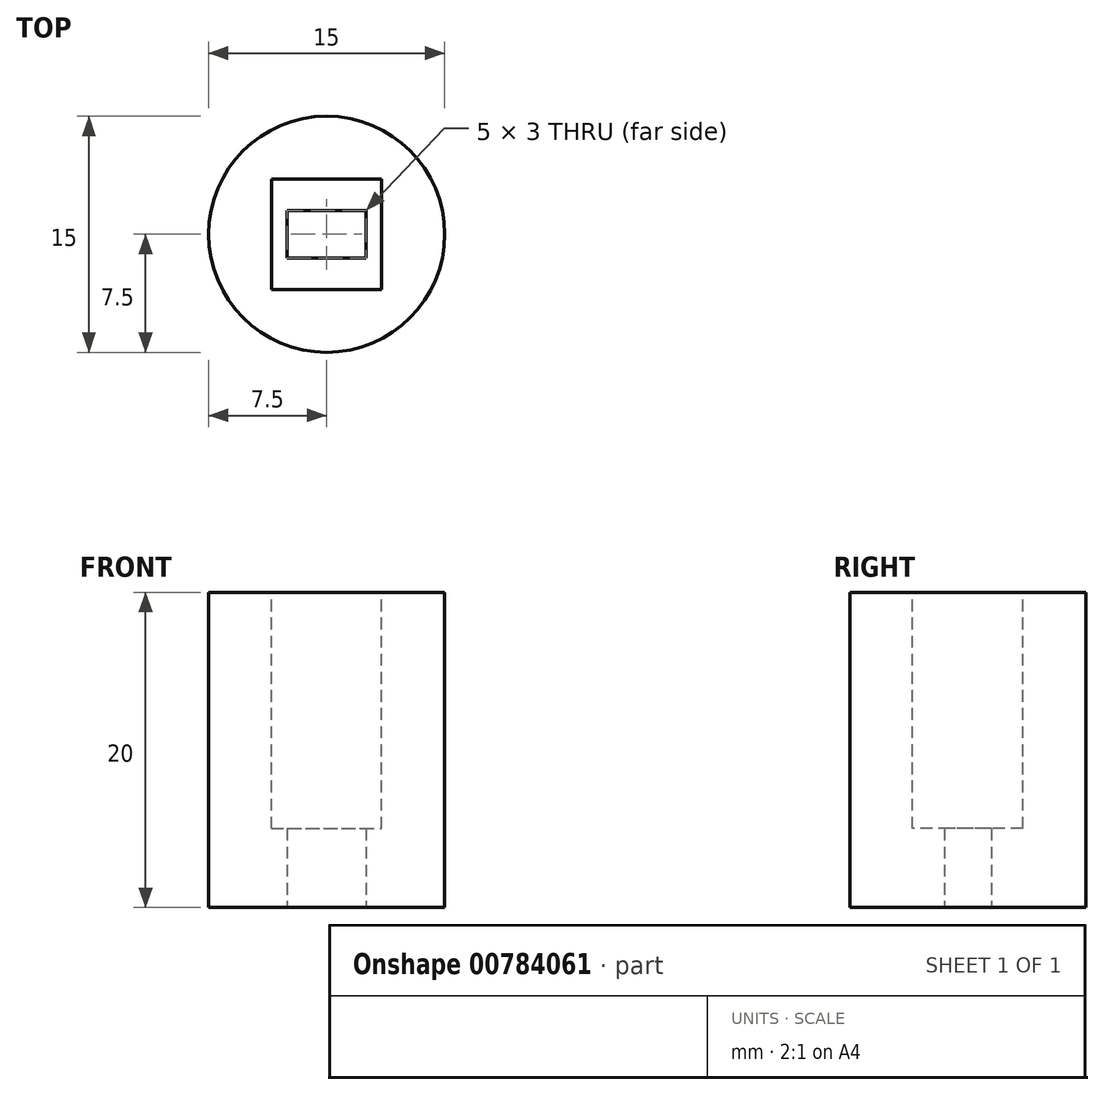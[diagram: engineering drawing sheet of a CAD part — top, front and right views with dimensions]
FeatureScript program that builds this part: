
annotation { "Feature Type Name" : "Feature", "Feature Type Description" : "" }
export const myFeature = defineFeature(function(context is Context, id is Id, definition is map)
    precondition{}
    {
        {
            var Q0;
            Q0=qCreatedBy(makeId("Top.planeOp"),FACE);
            var sketch = newSketch(context, id + "F0", { "sketchPlane" : qUnion([Q0])});
            skCircle(sketch, "E0", {"center": v(0, 0) * mm, "radius": 7.5 * mm});
            skLineSegment(sketch, "E1.bottom", {"start": v(-2.5, 1.5) * mm, "end": v(2.5, 1.5) * mm});
            skLineSegment(sketch, "E1.top", {"start": v(-2.5, -1.5) * mm, "end": v(2.5, -1.5) * mm});
            skLineSegment(sketch, "E1.left", {"start": v(-2.5, 1.5) * mm, "end": v(-2.5, -1.5) * mm});
            skLineSegment(sketch, "E1.right", {"start": v(2.5, 1.5) * mm, "end": v(2.5, -1.5) * mm});
            skSolve(sketch);
        }
        {
            var Q0;
            Q0=makeQuery(id+"F0.imprint","IMPRINT",FACE,{"disambiguationData":[TD([[makeQuery(id+"F0.imprint","IMPRINT",EDGE,{"derivedFrom":sQuery(id+"F0.wireOp",EDGE,"E0")}),1.0]])]});
            extrude(context, id + "F1", {"entities" : qUnion([Q0]), "depth" : 20 * mm, "offsetDistance" : 25 * mm});
        }
        {
            var Q0;
            Q0=makeQuery(id+"F1.opExtrude","CAP_FACE",FACE,{"disambiguationData":[OSD([sQuery(id+"F0.wireOp",EDGE,"E0"),sQuery(id+"F0.wireOp",EDGE,"E1.bottom"),sQuery(id+"F0.wireOp",EDGE,"E1.top"),sQuery(id+"F0.wireOp",EDGE,"E1.left"),sQuery(id+"F0.wireOp",EDGE,"E1.right")])],"isStart":false});
            var sketch = newSketch(context, id + "F2", { "sketchPlane" : qUnion([Q0])});
            skLineSegment(sketch, "E2.bottom", {"start": v(-3.5, 3.5) * mm, "end": v(3.5, 3.5) * mm});
            skLineSegment(sketch, "E2.top", {"start": v(-3.5, -3.5) * mm, "end": v(3.5, -3.5) * mm});
            skLineSegment(sketch, "E2.left", {"start": v(-3.5, 3.5) * mm, "end": v(-3.5, -3.5) * mm});
            skLineSegment(sketch, "E2.right", {"start": v(3.5, 3.5) * mm, "end": v(3.5, -3.5) * mm});
            skSolve(sketch);
        }
        {
            var Q0;
            Q0=makeQuery(id+"F2.imprint","IMPRINT",FACE,{"disambiguationData":[TD([[makeQuery(id+"F2.imprint","IMPRINT",EDGE,{"derivedFrom":sQuery(id+"F2.wireOp",EDGE,"E2.bottom")}),-1.0]])]});
            extrude(context, id + "F3", {"entities" : qUnion([Q0]), "operationType" : NewBodyOperationType.REMOVE, "oppositeDirection" : true, "depth" : 15 * mm, "offsetDistance" : 25 * mm});
        }
    });
